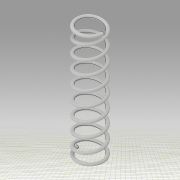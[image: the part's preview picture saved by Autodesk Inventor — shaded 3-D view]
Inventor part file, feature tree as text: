
AUTODESK INVENTOR PART (.ipt)
format: ipt  version: 2018 (Build 220112000, 112)  size: 403,968 bytes
history: native  units: in
note: dims shown in document units (in); Inventor stores cm internally (conversion verified against a paired STEP export)
features: helix x1, sketch x1
ambient origin geometry x8: Origin, YZ Plane, XZ Plane, XY Plane, X Axis, Y Axis, Z Axis, Center Point
bodies: Solid1 (feature_tree)
feature tree (2):
  helix  "Coil1"  [1 undecoded]
  sketch  "Sketch1"  dims[d1=0.147in d2=1.0in d3=1.15in d4=3.1496in d5=0.0in d6=90.0deg d7=180.0deg d8=90.0deg d9=180.0deg]
note: 1 required parameter value undecoded (feature->parameter linkage not recoverable at this tier; creation-order binding heuristic only, values carry confidence <= 0.55)
